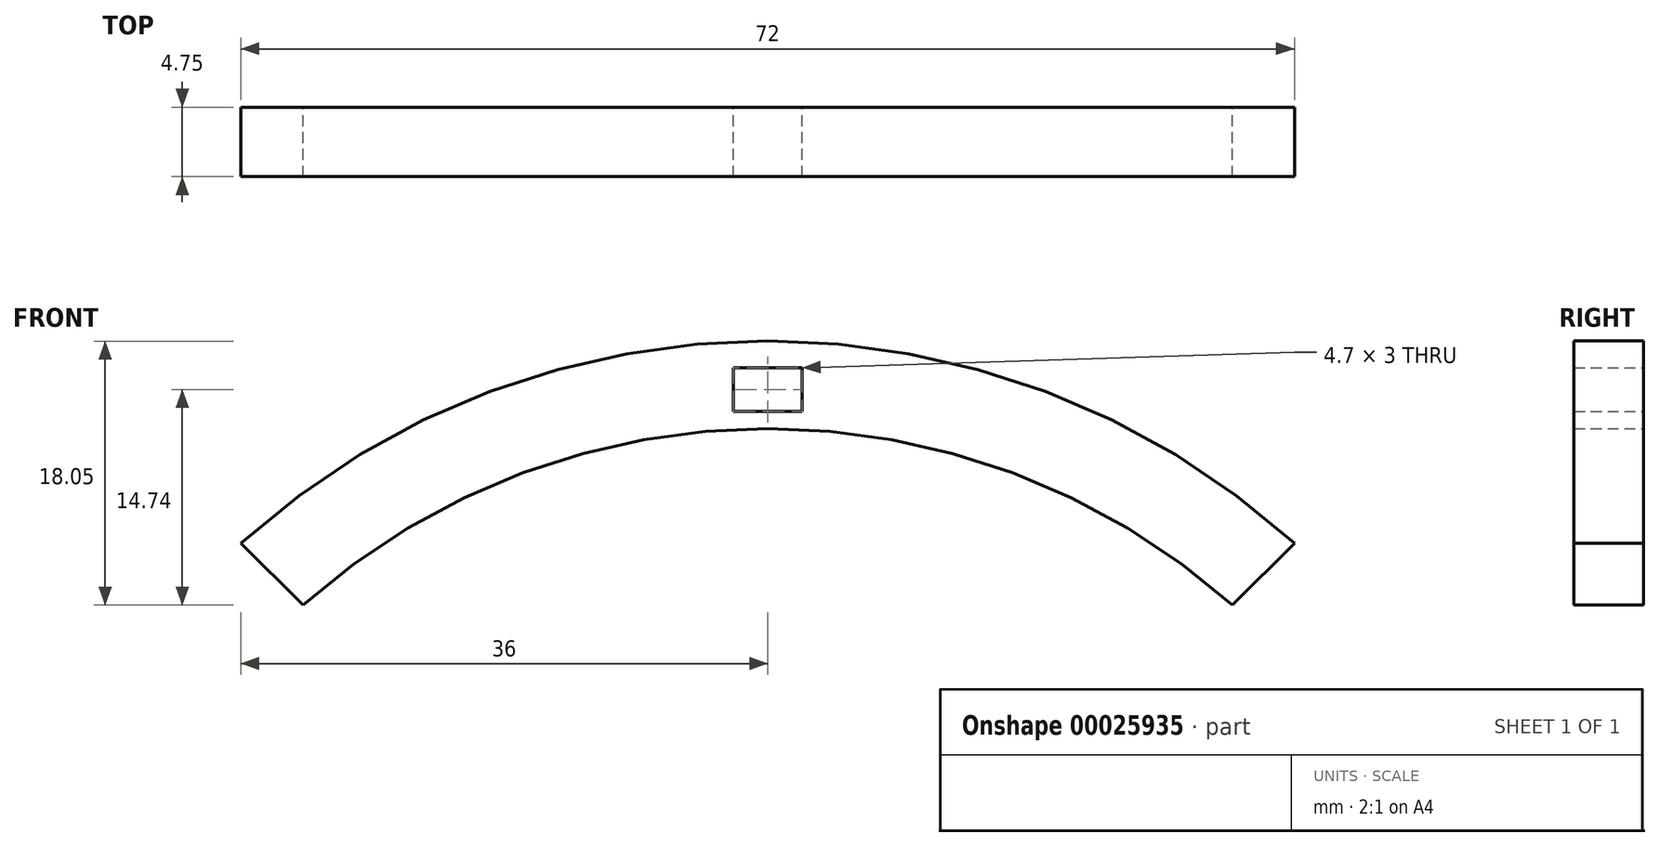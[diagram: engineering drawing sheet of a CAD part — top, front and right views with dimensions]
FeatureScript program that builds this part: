
annotation { "Feature Type Name" : "Feature", "Feature Type Description" : "" }
export const myFeature = defineFeature(function(context is Context, id is Id, definition is map)
    precondition{}
    {
        {
            var Q0;
            Q0=qCreatedBy(makeId("Front.planeOp"),FACE);
            var sketch = newSketch(context, id + "F0", { "sketchPlane" : qUnion([Q0])});
            skLineSegment(sketch, "E0.bottom", {"start": v(0, 0) * mm, "end": v(66.5, 0) * mm, "construction": true});
            skLineSegment(sketch, "E0.top", {"start": v(0, 38) * mm, "end": v(66.5, 38) * mm, "construction": true});
            skLineSegment(sketch, "E0.left", {"start": v(0, 0) * mm, "end": v(0, 23.25) * mm, "construction": true});
            skLineSegment(sketch, "E0.right", {"start": v(66.5, 0) * mm, "end": v(66.5, 38) * mm, "construction": true});
            skLineSegment(sketch, "E1", {"start": v(-4, -8) * mm, "end": v(48.64, -8) * mm, "construction": true});
            skLineSegment(sketch, "E2", {"start": v(48.64, -8) * mm, "end": v(52.64, -4) * mm, "construction": true});
            skLineSegment(sketch, "E3", {"start": v(52.64, -4) * mm, "end": v(102.5, -4) * mm, "construction": true});
            skLineSegment(sketch, "E4", {"start": v(102.5, -4) * mm, "end": v(110.5, -12) * mm, "construction": true});
            skLineSegment(sketch, "E5", {"start": v(110.5, -12) * mm, "end": v(132.04, -12) * mm, "construction": true});
            skLineSegment(sketch, "E6", {"start": v(70.39, 50) * mm, "end": v(-4, 50) * mm, "construction": true});
            skArc(sketch, "E7", {"start": v(-4, 50) * mm, "mid": v(-8.51, 47.97) * mm, "end": v(-10, 43.26) * mm, "construction": true});
            skLineSegment(sketch, "E8", {"start": v(-10, 43.26) * mm, "end": v(-4, -8) * mm, "construction": true});
            skCircle(sketch, "E9", {"center": v(127.5, -4) * mm, "radius": 5 * mm, "construction": true});
            skLineSegment(sketch, "E10", {"start": v(70.39, 50) * mm, "end": v(73.77, 46.62) * mm, "construction": true});
            skLineSegment(sketch, "E11", {"start": v(73.77, 46.62) * mm, "end": v(73.77, 0) * mm, "construction": true});
            skLineSegment(sketch, "E12", {"start": v(73.77, 0) * mm, "end": v(102.5, 0) * mm, "construction": true});
            skLineSegment(sketch, "E13", {"start": v(102.5, 0) * mm, "end": v(102.5, 36) * mm, "construction": true});
            skLineSegment(sketch, "E14", {"start": v(135.38, 30) * mm, "end": v(135.38, -8.67) * mm, "construction": true});
            skLineSegment(sketch, "E15", {"start": v(135.38, -8.67) * mm, "end": v(132.04, -12) * mm, "construction": true});
            skLineSegment(sketch, "E16.bottom", {"start": v(-1.5, 38) * mm, "end": v(-6.25, 38) * mm, "construction": true});
            skLineSegment(sketch, "E16.top", {"start": v(-1.5, 33.25) * mm, "end": v(-6.25, 33.25) * mm, "construction": true});
            skLineSegment(sketch, "E16.left", {"start": v(-1.5, 38) * mm, "end": v(-1.5, 33.25) * mm, "construction": true});
            skLineSegment(sketch, "E16.right", {"start": v(-6.25, 38) * mm, "end": v(-6.25, 33.25) * mm, "construction": true});
            skLineSegment(sketch, "E17.bottom", {"start": v(110.75, 3.75) * mm, "end": v(115.5, 3.75) * mm, "construction": true});
            skLineSegment(sketch, "E17.top", {"start": v(110.75, -1) * mm, "end": v(115.5, -1) * mm, "construction": true});
            skLineSegment(sketch, "E17.left", {"start": v(110.75, 3.75) * mm, "end": v(110.75, -1) * mm, "construction": true});
            skLineSegment(sketch, "E17.right", {"start": v(115.5, 3.75) * mm, "end": v(115.5, -1) * mm, "construction": true});
            skLineSegment(sketch, "E18", {"start": v(0, 28) * mm, "end": v(-4.75, 28) * mm, "construction": true});
            skLineSegment(sketch, "E19", {"start": v(-4.75, 28) * mm, "end": v(-4.75, 23.25) * mm, "construction": true});
            skLineSegment(sketch, "E20", {"start": v(-4.75, 23.25) * mm, "end": v(0, 23.25) * mm, "construction": true});
            skLineSegment(sketch, "E21.trimOffspring", {"start": v(0, 28) * mm, "end": v(0, 38) * mm, "construction": true});
            skLineSegment(sketch, "E22", {"start": v(102.5, 0) * mm, "end": v(86.5, 0) * mm, "construction": true});
            skLineSegment(sketch, "E23", {"start": v(86.5, 0) * mm, "end": v(86.5, -4) * mm, "construction": true});
            skLineSegment(sketch, "E24", {"start": v(86.5, -4) * mm, "end": v(102.5, -4) * mm, "construction": true});
            skLineSegment(sketch, "E25", {"start": v(102.5, 0) * mm, "end": v(102.5, -4) * mm, "construction": true});
            skLineSegment(sketch, "E26", {"start": v(102.5, 36) * mm, "end": v(91.5, 47) * mm, "construction": true});
            skArc(sketch, "E27", {"start": v(91.5, 47) * mm, "mid": v(127.5, 60.81) * mm, "end": v(163.5, 47) * mm});
            skLineSegment(sketch, "E28", {"start": v(163.5, 47) * mm, "end": v(146.5, 30) * mm, "construction": true});
            skLineSegment(sketch, "E29", {"start": v(146.5, 30) * mm, "end": v(135.38, 30) * mm, "construction": true});
            skLineSegment(sketch, "E30.rect.bottom", {"start": v(125.15, 59) * mm, "end": v(129.85, 59) * mm});
            skLineSegment(sketch, "E30.rect.top", {"start": v(125.15, 56) * mm, "end": v(129.85, 56) * mm});
            skLineSegment(sketch, "E30.rect.left", {"start": v(125.15, 59) * mm, "end": v(125.15, 56) * mm});
            skLineSegment(sketch, "E30.rect.right", {"start": v(129.85, 59) * mm, "end": v(129.85, 56) * mm});
            skPoint(sketch, "E30.rect.middle", {"position": v(127.5, 57.5) * mm});
            skLineSegment(sketch, "E31", {"start": v(91.5, 47) * mm, "end": v(95.74, 42.76) * mm});
            skArc(sketch, "E32", {"start": v(95.74, 42.76) * mm, "mid": v(127.5, 54.82) * mm, "end": v(159.26, 42.76) * mm});
            skLineSegment(sketch, "E33", {"start": v(159.26, 42.76) * mm, "end": v(163.5, 47) * mm});
            skSolve(sketch);
        }
        {
            var Q0;
            Q0=qSketchRegion(id+"F0",true);
            extrude(context, id + "F1", {"entities" : qUnion([Q0]), "depth" : 4.75 * mm});
        }
    });
